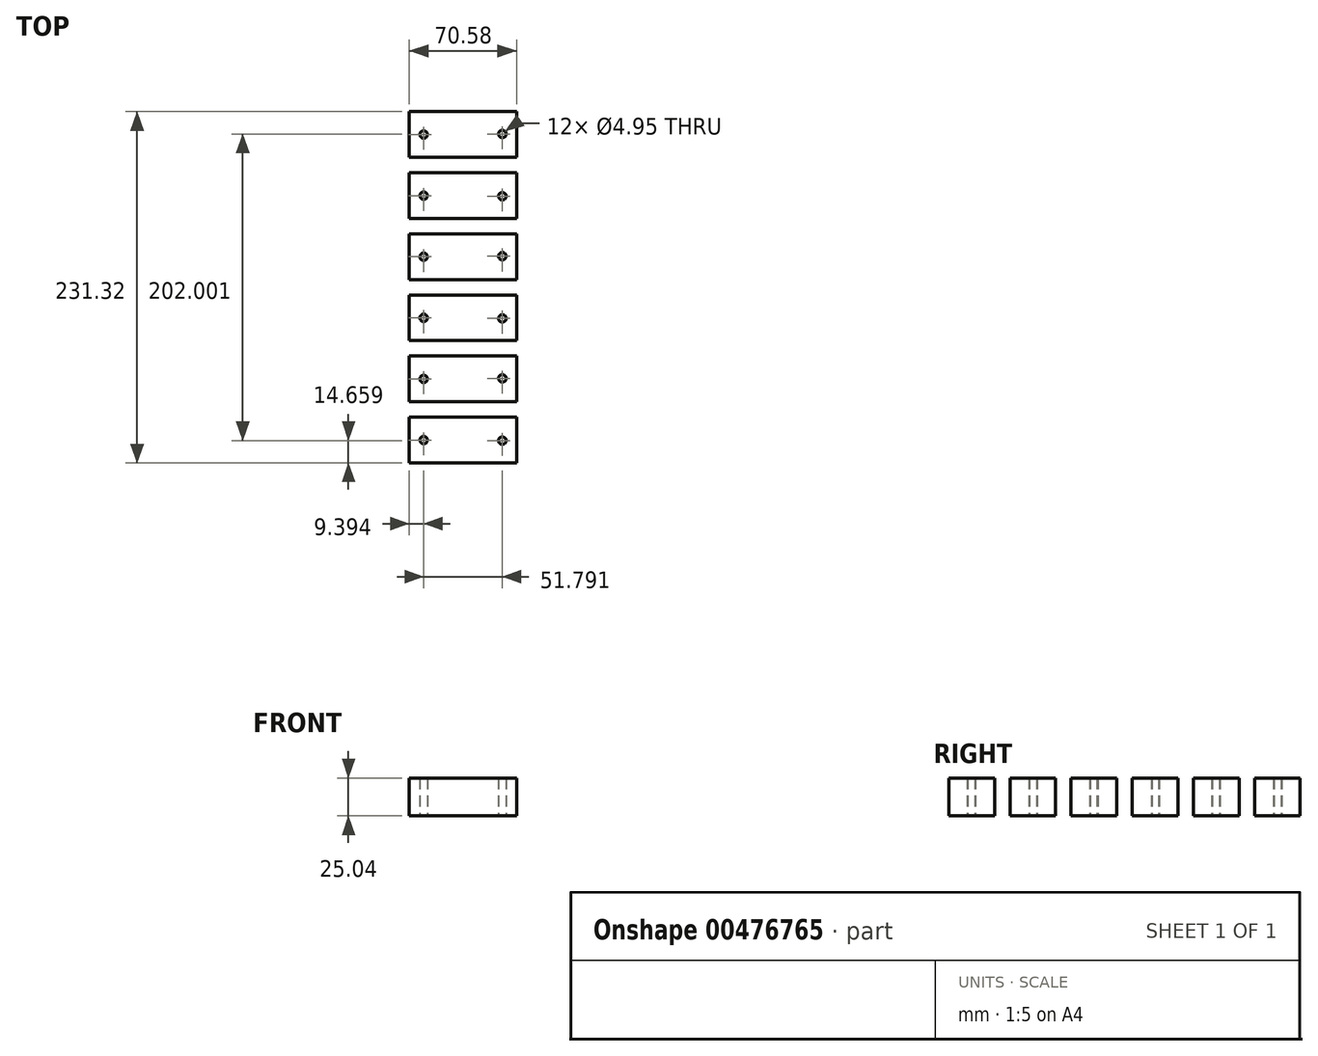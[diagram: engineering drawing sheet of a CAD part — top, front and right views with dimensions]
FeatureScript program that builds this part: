
annotation { "Feature Type Name" : "Feature", "Feature Type Description" : "" }
export const myFeature = defineFeature(function(context is Context, id is Id, definition is map)
    precondition{}
    {
        {
            var Q0;
            Q0=qCreatedBy(makeId("Top.planeOp"),FACE);
            var sketch = newSketch(context, id + "F0", { "sketchPlane" : qUnion([Q0])});
            skLineSegment(sketch, "E0.bottom", {"start": v(-41.17, 5.73) * mm, "end": v(29.41, 5.73) * mm});
            skLineSegment(sketch, "E0.top", {"start": v(-41.17, -24.36) * mm, "end": v(29.41, -24.36) * mm});
            skLineSegment(sketch, "E0.left", {"start": v(-41.17, 5.73) * mm, "end": v(-41.17, -24.36) * mm});
            skLineSegment(sketch, "E0.right", {"start": v(29.41, 5.73) * mm, "end": v(29.41, -24.36) * mm});
            skCircle(sketch, "E1", {"center": v(-31.78, -9.31) * mm, "radius": 2.48 * mm});
            skPoint(sketch, "E2.orphan", {"position": v(29.41, -9.31) * mm});
            skLineSegment(sketch, "E3", {"start": v(-31.78, -9.31) * mm, "end": v(-29.3, -9.31) * mm, "construction": true});
            skPoint(sketch, "E4.start.orphan", {"position": v(-41.17, -9.31) * mm});
            skPoint(sketch, "E5.start.orphan", {"position": v(-34.25, -9.31) * mm});
            skCircle(sketch, "E6.MirrorC", {"center": v(20.01, -9.7) * mm, "radius": 2.48 * mm});
            skLineSegment(sketch, "E7", {"start": v(-47.2, -29.44) * mm, "end": v(44.7, -29.44) * mm, "construction": true});
            skLineSegment(sketch, "E8", {"start": v(-41.17, -24.36) * mm, "end": v(-41.17, -29.44) * mm, "construction": true});
            skLineSegment(sketch, "E9", {"start": v(-47.36, 10.8) * mm, "end": v(44.22, 10.8) * mm, "construction": true});
            skLineSegment(sketch, "E10", {"start": v(-41.17, 5.73) * mm, "end": v(-41.17, 10.8) * mm, "construction": true});
            skLineSegment(sketch, "E11.MirrorCS", {"start": v(-31.78, -49.56) * mm, "end": v(-29.3, -49.56) * mm, "construction": true});
            skLineSegment(sketch, "E12.MirrorCS", {"start": v(-41.17, -64.6) * mm, "end": v(-41.17, -69.68) * mm, "construction": true});
            skCircle(sketch, "E13.MirrorC", {"center": v(-31.78, -49.56) * mm, "radius": 2.48 * mm});
            skCircle(sketch, "E14.MirrorC", {"center": v(20.01, -49.18) * mm, "radius": 2.48 * mm});
            skLineSegment(sketch, "E15.MirrorCS", {"start": v(-41.17, -64.6) * mm, "end": v(29.41, -64.6) * mm});
            skPoint(sketch, "E16.MirrorP", {"position": v(-41.17, -49.56) * mm});
            skLineSegment(sketch, "E17.MirrorCS", {"start": v(29.41, -64.6) * mm, "end": v(29.41, -34.52) * mm});
            skPoint(sketch, "E18.MirrorP", {"position": v(29.41, -49.56) * mm});
            skLineSegment(sketch, "E19.MirrorCS", {"start": v(-41.17, -34.52) * mm, "end": v(29.41, -34.52) * mm});
            skPoint(sketch, "E20.MirrorP", {"position": v(-34.25, -49.56) * mm});
            skLineSegment(sketch, "E21.MirrorCS", {"start": v(-47.36, -69.68) * mm, "end": v(44.22, -69.68) * mm, "construction": true});
            skLineSegment(sketch, "E22.MirrorCS", {"start": v(-41.17, -64.6) * mm, "end": v(-41.17, -34.52) * mm});
            skLineSegment(sketch, "E23.MirrorCS", {"start": v(-31.78, -89.8) * mm, "end": v(-29.3, -89.8) * mm, "construction": true});
            skCircle(sketch, "E24.MirrorC", {"center": v(-31.78, -89.8) * mm, "radius": 2.48 * mm});
            skCircle(sketch, "E25.MirrorC", {"center": v(20.01, -90.2) * mm, "radius": 2.48 * mm});
            skLineSegment(sketch, "E26.MirrorCS", {"start": v(29.41, -74.76) * mm, "end": v(29.41, -104.85) * mm});
            skPoint(sketch, "E27.MirrorP", {"position": v(-41.17, -89.8) * mm});
            skPoint(sketch, "E28.MirrorP", {"position": v(-34.25, -89.8) * mm});
            skLineSegment(sketch, "E29.MirrorCS", {"start": v(-47.2, -109.93) * mm, "end": v(44.7, -109.93) * mm, "construction": true});
            skLineSegment(sketch, "E30.MirrorCS", {"start": v(-41.17, -74.76) * mm, "end": v(29.41, -74.76) * mm});
            skLineSegment(sketch, "E31.MirrorCS", {"start": v(-41.17, -104.85) * mm, "end": v(29.41, -104.85) * mm});
            skLineSegment(sketch, "E32.MirrorCS", {"start": v(-41.17, -74.76) * mm, "end": v(-41.17, -104.85) * mm});
            skPoint(sketch, "E33.MirrorP", {"position": v(29.41, -89.8) * mm});
            skLineSegment(sketch, "E34.MirrorCS", {"start": v(-31.78, 30.93) * mm, "end": v(-29.3, 30.93) * mm, "construction": true});
            skLineSegment(sketch, "E35.MirrorCS", {"start": v(-41.17, 45.98) * mm, "end": v(-41.17, 51.06) * mm, "construction": true});
            skCircle(sketch, "E36.MirrorC", {"center": v(-31.78, 30.93) * mm, "radius": 2.48 * mm});
            skPoint(sketch, "E37.MirrorP", {"position": v(-41.17, 30.93) * mm});
            skLineSegment(sketch, "E38.MirrorCS", {"start": v(-41.17, 45.98) * mm, "end": v(29.41, 45.98) * mm});
            skLineSegment(sketch, "E39.MirrorCS", {"start": v(-41.17, 15.89) * mm, "end": v(29.41, 15.89) * mm});
            skLineSegment(sketch, "E40.MirrorCS", {"start": v(-47.2, 51.06) * mm, "end": v(44.7, 51.06) * mm, "construction": true});
            skCircle(sketch, "E41.MirrorC", {"center": v(20.01, 31.32) * mm, "radius": 2.48 * mm});
            skLineSegment(sketch, "E42.MirrorCS", {"start": v(29.41, 15.89) * mm, "end": v(29.41, 45.98) * mm});
            skPoint(sketch, "E43.MirrorP", {"position": v(-34.25, 30.93) * mm});
            skLineSegment(sketch, "E44.MirrorCS", {"start": v(-41.17, 15.89) * mm, "end": v(-41.17, 45.98) * mm});
            skPoint(sketch, "E45.MirrorP", {"position": v(29.41, 30.93) * mm});
            skCircle(sketch, "E46.MirrorC", {"center": v(-31.78, 71.18) * mm, "radius": 2.48 * mm});
            skLineSegment(sketch, "E47.MirrorCS", {"start": v(-31.78, 71.18) * mm, "end": v(-29.3, 71.18) * mm, "construction": true});
            skLineSegment(sketch, "E48.MirrorCS", {"start": v(-41.17, 96.38) * mm, "end": v(-41.17, 91.3) * mm, "construction": true});
            skLineSegment(sketch, "E49.MirrorCS", {"start": v(-41.17, 56.14) * mm, "end": v(-41.17, 51.06) * mm, "construction": true});
            skCircle(sketch, "E50.MirrorC", {"center": v(20.01, 70.8) * mm, "radius": 2.48 * mm});
            skLineSegment(sketch, "E51.MirrorCS", {"start": v(-41.17, 56.14) * mm, "end": v(29.41, 56.14) * mm});
            skPoint(sketch, "E52.MirrorP", {"position": v(-34.25, 71.18) * mm});
            skLineSegment(sketch, "E53.MirrorCS", {"start": v(-47.36, 91.3) * mm, "end": v(44.22, 91.3) * mm, "construction": true});
            skPoint(sketch, "E54.MirrorP", {"position": v(29.41, 71.18) * mm});
            skLineSegment(sketch, "E55.MirrorCS", {"start": v(-41.17, 86.22) * mm, "end": v(29.41, 86.22) * mm});
            skLineSegment(sketch, "E56.MirrorCS", {"start": v(29.41, 86.22) * mm, "end": v(29.41, 56.14) * mm});
            skPoint(sketch, "E57.MirrorP", {"position": v(-41.17, 71.18) * mm});
            skLineSegment(sketch, "E58.MirrorCS", {"start": v(-41.17, 86.22) * mm, "end": v(-41.17, 56.14) * mm});
            skLineSegment(sketch, "E59.MirrorCS", {"start": v(-41.17, 136.63) * mm, "end": v(-41.17, 131.55) * mm, "construction": true});
            skLineSegment(sketch, "E60.MirrorCS", {"start": v(-41.17, 126.47) * mm, "end": v(-41.17, 131.55) * mm, "construction": true});
            skLineSegment(sketch, "E61.MirrorCS", {"start": v(-31.78, 111.43) * mm, "end": v(-29.3, 111.43) * mm, "construction": true});
            skCircle(sketch, "E62.MirrorC", {"center": v(-31.78, 111.43) * mm, "radius": 2.48 * mm});
            skCircle(sketch, "E63.MirrorC", {"center": v(20.01, 111.8) * mm, "radius": 2.48 * mm});
            skPoint(sketch, "E64.MirrorP", {"position": v(-41.17, 111.43) * mm});
            skLineSegment(sketch, "E65.MirrorCS", {"start": v(-47.2, 131.55) * mm, "end": v(44.7, 131.55) * mm, "construction": true});
            skLineSegment(sketch, "E66.MirrorCS", {"start": v(-41.17, 126.47) * mm, "end": v(29.41, 126.47) * mm});
            skLineSegment(sketch, "E67.MirrorCS", {"start": v(-41.17, 96.38) * mm, "end": v(-41.17, 126.47) * mm});
            skLineSegment(sketch, "E68.MirrorCS", {"start": v(29.41, 96.38) * mm, "end": v(29.41, 126.47) * mm});
            skPoint(sketch, "E69.MirrorP", {"position": v(-34.25, 111.43) * mm});
            skPoint(sketch, "E70.MirrorP", {"position": v(29.41, 111.43) * mm});
            skLineSegment(sketch, "E71.MirrorCS", {"start": v(-41.17, 96.38) * mm, "end": v(29.41, 96.38) * mm});
            skSolve(sketch);
        }
        {
            var Q0;
            Q0 = qSketchRegion(id + "F0", true);
            extrude(context, id + "F1", {"entities" : qUnion([Q0]), "depth" : 25.04 * mm});
        }
    });
